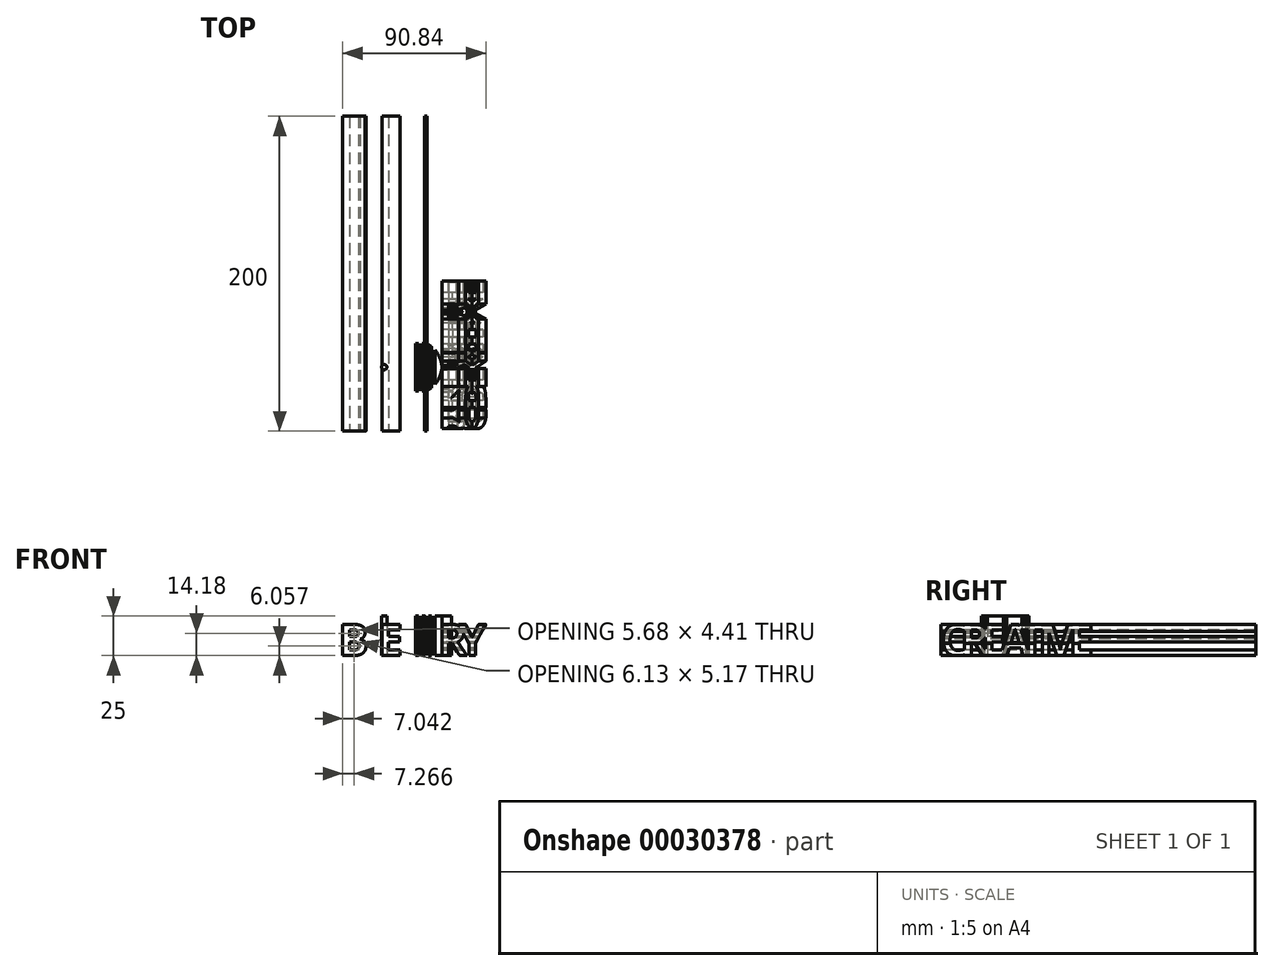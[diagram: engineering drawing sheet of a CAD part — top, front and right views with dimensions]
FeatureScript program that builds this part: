
annotation { "Feature Type Name" : "Feature", "Feature Type Description" : "" }
export const myFeature = defineFeature(function(context is Context, id is Id, definition is map)
    precondition{}
    {
        {
            var Q0;
            Q0=qCreatedBy(makeId("Front.planeOp"),FACE);
            var sketch = newSketch(context, id + "F0", { "sketchPlane" : qUnion([Q0])});
            skText(sketch, "E0", { "text": "B", "fontName": "OpenSans-Bold.ttf"});
            skText(sketch, "E1", { "text": "E", "fontName": "OpenSans-Bold.ttf"});
            skText(sketch, "E2", { "text": "E", "fontName": "OpenSans-Bold.ttf"});
            skText(sketch, "E3", { "text": "V", "fontName": "OpenSans-Bold.ttf"});
            skText(sketch, "E4", { "text": "E", "fontName": "OpenSans-Bold.ttf"});
            skText(sketch, "E5", { "text": "R", "fontName": "OpenSans-Bold.ttf"});
            skText(sketch, "E6", { "text": "Y", "fontName": "OpenSans-Bold.ttf"});
            const initialGuessF0  = {"E0": [0, 0, 1, 0, 0.02], "E1": [0.014, 0, 1, 0, 0.02], "E2": [0.025, 0, 1, 0, 0.02], "E3": [0.038, 0, 1, 0, 0.02], "E4": [0.052, 0, 1, 0, 0.02], "E5": [0.063, 0, 1, 0, 0.02], "E6": [0.076, 0, 1, 0, 0.02]};
            skSetInitialGuess(sketch, initialGuessF0);
            skSolve(sketch);
        }
        {
            var Q0;
            Q0=makeQuery(id+"F0.imprint","IMPRINT",FACE,{"disambiguationData":[TD([[makeQuery(id+"F0.imprint","IMPRINT",EDGE,{"derivedFrom":sQuery(id+"F0.wireOp",EDGE,"E0.sketch_text.stroke-0")}),-1.0]])]});
            var Q1;
            {var subQ7=sQuery(id+"F0.wireOp",EDGE,"E1.sketch_text.stroke-0");Q1=makeQuery(id+"F0.imprint","IMPRINT",FACE,{"disambiguationData":[TD([[makeQuery(id+"F0.imprint","IMPRINT",EDGE,{"derivedFrom":subQ7}),-1.0]])]});}
            var Q2;
            {var subQ1=sQuery(id+"F0.wireOp",EDGE,"E0.sketch_text.stroke-7");var subQ3=sQuery(id+"F0.wireOp",EDGE,"E0.sketch_text.stroke-8");var subQ5=makeQuery(id+"F0.imprint","INTERSECT",VERTEX,{"derivedFrom":[subQ1,subQ3]});Q2=makeQuery(id+"F0.imprint","IMPRINT",FACE,{"disambiguationData":[TD([[makeQuery(id+"F0.imprint","IMPRINT",EDGE,{"disambiguationData":[TD([[subQ5,1.0]])],"derivedFrom":subQ1}),-1.0]])]});}
            var Q3;
            {var subQ1=sQuery(id+"F0.wireOp",EDGE,"E0.sketch_text.stroke-3");var subQ3=sQuery(id+"F0.wireOp",EDGE,"E0.sketch_text.stroke-2");var subQ5=makeQuery(id+"F0.imprint","INTERSECT",VERTEX,{"derivedFrom":[subQ3,subQ1]});Q3=makeQuery(id+"F0.imprint","IMPRINT",FACE,{"disambiguationData":[TD([[makeQuery(id+"F0.imprint","IMPRINT",EDGE,{"disambiguationData":[TD([[subQ5,1.0]])],"derivedFrom":subQ3}),-1.0]])]});}
            var Q4;
            {var subQ7=sQuery(id+"F0.wireOp",EDGE,"E1.sketch_text.stroke-3");Q4=makeQuery(id+"F0.imprint","IMPRINT",FACE,{"disambiguationData":[TD([[makeQuery(id+"F0.imprint","IMPRINT",EDGE,{"derivedFrom":subQ7}),1.0]])]});}
            var Q5;
            {var subQ1=sQuery(id+"F0.wireOp",EDGE,"E1.sketch_text.stroke-3");Q5=makeQuery(id+"F0.imprint","IMPRINT",FACE,{"disambiguationData":[TD([[makeQuery(id+"F0.imprint","IMPRINT",EDGE,{"derivedFrom":subQ1}),-1.0]])]});}
            var Q6;
            {var subQ5=sQuery(id+"F0.wireOp",EDGE,"E1.sketch_text.stroke-11");Q6=makeQuery(id+"F0.imprint","IMPRINT",FACE,{"disambiguationData":[TD([[makeQuery(id+"F0.imprint","IMPRINT",EDGE,{"derivedFrom":subQ5}),-1.0]])]});}
            var Q7;
            {var subQ3=sQuery(id+"F0.wireOp",EDGE,"E3.sketch_text.stroke-0");Q7=makeQuery(id+"F0.imprint","IMPRINT",FACE,{"disambiguationData":[TD([[makeQuery(id+"F0.imprint","IMPRINT",EDGE,{"derivedFrom":subQ3}),-1.0]])]});}
            var Q8;
            {var subQ0=sQuery(id+"F0.wireOp",EDGE,"E3.sketch_text.stroke-4");var subQ1=sQuery(id+"F0.wireOp",EDGE,"E2.sketch_text.stroke-3");var subQ2=makeQuery(id+"F0.imprint","INTERSECT",VERTEX,{"derivedFrom":[subQ1,subQ0]});Q8=makeQuery(id+"F0.imprint","IMPRINT",FACE,{"disambiguationData":[TD([[makeQuery(id+"F0.imprint","IMPRINT",EDGE,{"disambiguationData":[TD([[subQ2,-1.0]])],"derivedFrom":subQ1}),-1.0]])]});}
            var Q9;
            {var subQ0=sQuery(id+"F0.wireOp",EDGE,"E4.sketch_text.stroke-2");var subQ1=sQuery(id+"F0.wireOp",EDGE,"E3.sketch_text.stroke-1");var subQ2=makeQuery(id+"F0.imprint","INTERSECT",VERTEX,{"derivedFrom":[subQ1,subQ0]});Q9=makeQuery(id+"F0.imprint","IMPRINT",FACE,{"disambiguationData":[TD([[makeQuery(id+"F0.imprint","IMPRINT",EDGE,{"disambiguationData":[TD([[subQ2,-1.0]])],"derivedFrom":subQ1}),-1.0]])]});}
            var Q10;
            {var subQ7=sQuery(id+"F0.wireOp",EDGE,"E4.sketch_text.stroke-0");Q10=makeQuery(id+"F0.imprint","IMPRINT",FACE,{"disambiguationData":[TD([[makeQuery(id+"F0.imprint","IMPRINT",EDGE,{"derivedFrom":subQ7}),-1.0]])]});}
            var Q11;
            {var subQ1=sQuery(id+"F0.wireOp",EDGE,"E4.sketch_text.stroke-3");Q11=makeQuery(id+"F0.imprint","IMPRINT",FACE,{"disambiguationData":[TD([[makeQuery(id+"F0.imprint","IMPRINT",EDGE,{"derivedFrom":subQ1}),-1.0]])]});}
            var Q12;
            {var subQ0=sQuery(id+"F0.wireOp",EDGE,"E4.sketch_text.stroke-3");Q12=makeQuery(id+"F0.imprint","IMPRINT",FACE,{"disambiguationData":[TD([[makeQuery(id+"F0.imprint","IMPRINT",EDGE,{"derivedFrom":subQ0}),1.0]])]});}
            var Q13;
            {var subQ5=sQuery(id+"F0.wireOp",EDGE,"E4.sketch_text.stroke-11");Q13=makeQuery(id+"F0.imprint","IMPRINT",FACE,{"disambiguationData":[TD([[makeQuery(id+"F0.imprint","IMPRINT",EDGE,{"derivedFrom":subQ5}),-1.0]])]});}
            var Q14;
            {var subQ3=sQuery(id+"F0.wireOp",EDGE,"E5.sketch_text.stroke-12");Q14=makeQuery(id+"F0.imprint","IMPRINT",FACE,{"disambiguationData":[TD([[makeQuery(id+"F0.imprint","IMPRINT",EDGE,{"derivedFrom":subQ3}),-1.0]])]});}
            var Q15;
            {var subQ7=sQuery(id+"F0.wireOp",EDGE,"E5.sketch_text.stroke-12");Q15=makeQuery(id+"F0.imprint","IMPRINT",FACE,{"disambiguationData":[TD([[makeQuery(id+"F0.imprint","IMPRINT",EDGE,{"derivedFrom":subQ7}),1.0]])]});}
            extrude(context, id + "F1", {"entities" : qUnion([Q0, Q1, Q2, Q3, Q4, Q5, Q6, Q7, Q8, Q9, Q10, Q11, Q12, Q13, Q14, Q15]), "oppositeDirection" : true, "depth" : 200 * mm});
        }
        {
            var Q0;
            Q0=qCreatedBy(makeId("Right.planeOp"),FACE);
            var sketch = newSketch(context, id + "F2", { "sketchPlane" : qUnion([Q0])});
            skText(sketch, "E7", { "text": "C", "fontName": "OpenSans-Bold.ttf"});
            skText(sketch, "E8", { "text": "R", "fontName": "OpenSans-Bold.ttf"});
            skText(sketch, "E9", { "text": "E", "fontName": "OpenSans-Bold.ttf"});
            skText(sketch, "E10", { "text": "A", "fontName": "OpenSans-Bold.ttf"});
            skText(sketch, "E11", { "text": "T", "fontName": "OpenSans-Bold.ttf"});
            skText(sketch, "E12", { "text": "I", "fontName": "OpenSans-Bold.ttf"});
            skText(sketch, "E13", { "text": "V", "fontName": "OpenSans-Bold.ttf"});
            skText(sketch, "E14", { "text": "E", "fontName": "OpenSans-Bold.ttf"});
            const initialGuessF2  = {"E7": [0, 0, 1, 0, 0.02], "E8": [0.01265, 0, 1, 0, 0.02], "E9": [0.02573, 0, 1, 0, 0.02], "E10": [0.03756, 0, 1, 0, 0.02], "E11": [0.04955, 0, 1, 0, 0.02], "E12": [0.062, 0, 1, 0, 0.02], "E13": [0.06685, 0, 1, 0, 0.02], "E14": [0.0813, 0, 1, 0, 0.02]};
            skSetInitialGuess(sketch, initialGuessF2);
            skSolve(sketch);
        }
        {
            var Q0;
            Q0 = qSketchRegion(id + "F2", true);
            var Q1;
            {var subQ5=sQuery(id+"F2.wireOp",EDGE,"E7.sketch_text.stroke-12");Q1=makeQuery(id+"F2.imprint","IMPRINT",FACE,{"disambiguationData":[TD([[makeQuery(id+"F2.imprint","IMPRINT",EDGE,{"derivedFrom":subQ5}),-1.0]])]});}
            var Q2;
            {var subQ1=sQuery(id+"F2.wireOp",EDGE,"E8.sketch_text.stroke-13");var subQ3=sQuery(id+"F2.wireOp",EDGE,"E8.sketch_text.stroke-12");var subQ5=makeQuery(id+"F2.imprint","INTERSECT",VERTEX,{"derivedFrom":[subQ3,subQ1]});Q2=makeQuery(id+"F2.imprint","IMPRINT",FACE,{"disambiguationData":[TD([[makeQuery(id+"F2.imprint","IMPRINT",EDGE,{"disambiguationData":[TD([[subQ5,1.0]])],"derivedFrom":subQ3}),-1.0]])]});}
            extrude(context, id + "F3", {"entities" : qUnion([Q0, Q1, Q2]), "depth" : 200 * mm});
        }
        {
            var Q0;
            Q0=makeQuery(id+"F1.opExtrude","SWEPT_BODY",BODY,{"disambiguationData":[OSD([sQuery(id+"F0.wireOp",EDGE,"E0.sketch_text.stroke-0"),sQuery(id+"F0.wireOp",EDGE,"E0.sketch_text.stroke-1"),sQuery(id+"F0.wireOp",EDGE,"E0.sketch_text.stroke-2"),sQuery(id+"F0.wireOp",EDGE,"E0.sketch_text.stroke-3"),sQuery(id+"F0.wireOp",EDGE,"E0.sketch_text.stroke-4"),sQuery(id+"F0.wireOp",EDGE,"E0.sketch_text.stroke-5"),sQuery(id+"F0.wireOp",EDGE,"E0.sketch_text.stroke-6"),sQuery(id+"F0.wireOp",EDGE,"E0.sketch_text.stroke-7"),sQuery(id+"F0.wireOp",EDGE,"E0.sketch_text.stroke-8"),sQuery(id+"F0.wireOp",EDGE,"E0.sketch_text.stroke-9"),sQuery(id+"F0.wireOp",EDGE,"E0.sketch_text.stroke-10"),sQuery(id+"F0.wireOp",EDGE,"E0.sketch_text.stroke-11"),sQuery(id+"F0.wireOp",EDGE,"E0.sketch_text.stroke-12"),sQuery(id+"F0.wireOp",EDGE,"E0.sketch_text.stroke-13"),sQuery(id+"F0.wireOp",EDGE,"E0.sketch_text.stroke-14"),sQuery(id+"F0.wireOp",EDGE,"E0.sketch_text.stroke-15"),sQuery(id+"F0.wireOp",EDGE,"E0.sketch_text.stroke-16"),sQuery(id+"F0.wireOp",EDGE,"E0.sketch_text.stroke-17"),sQuery(id+"F0.wireOp",EDGE,"E0.sketch_text.stroke-18"),sQuery(id+"F0.wireOp",EDGE,"E0.sketch_text.stroke-19"),sQuery(id+"F0.wireOp",EDGE,"E0.sketch_text.stroke-20"),sQuery(id+"F0.wireOp",EDGE,"E0.sketch_text.stroke-21"),sQuery(id+"F0.wireOp",EDGE,"E0.sketch_text.stroke-22"),sQuery(id+"F0.wireOp",EDGE,"E0.sketch_text.stroke-23"),sQuery(id+"F0.wireOp",EDGE,"E0.sketch_text.stroke-24"),sQuery(id+"F0.wireOp",EDGE,"E1.sketch_text.stroke-0"),sQuery(id+"F0.wireOp",EDGE,"E1.sketch_text.stroke-1"),sQuery(id+"F0.wireOp",EDGE,"E1.sketch_text.stroke-2"),sQuery(id+"F0.wireOp",EDGE,"E1.sketch_text.stroke-4"),sQuery(id+"F0.wireOp",EDGE,"E1.sketch_text.stroke-5"),sQuery(id+"F0.wireOp",EDGE,"E1.sketch_text.stroke-6"),sQuery(id+"F0.wireOp",EDGE,"E1.sketch_text.stroke-7"),sQuery(id+"F0.wireOp",EDGE,"E1.sketch_text.stroke-8"),sQuery(id+"F0.wireOp",EDGE,"E1.sketch_text.stroke-9"),sQuery(id+"F0.wireOp",EDGE,"E1.sketch_text.stroke-10"),sQuery(id+"F0.wireOp",EDGE,"E2.sketch_text.stroke-0"),sQuery(id+"F0.wireOp",EDGE,"E2.sketch_text.stroke-1"),sQuery(id+"F0.wireOp",EDGE,"E2.sketch_text.stroke-2"),sQuery(id+"F0.wireOp",EDGE,"E2.sketch_text.stroke-3"),sQuery(id+"F0.wireOp",EDGE,"E2.sketch_text.stroke-4"),sQuery(id+"F0.wireOp",EDGE,"E2.sketch_text.stroke-5"),sQuery(id+"F0.wireOp",EDGE,"E2.sketch_text.stroke-6"),sQuery(id+"F0.wireOp",EDGE,"E2.sketch_text.stroke-7"),sQuery(id+"F0.wireOp",EDGE,"E2.sketch_text.stroke-8"),sQuery(id+"F0.wireOp",EDGE,"E2.sketch_text.stroke-9"),sQuery(id+"F0.wireOp",EDGE,"E2.sketch_text.stroke-10"),sQuery(id+"F0.wireOp",EDGE,"E2.sketch_text.stroke-11"),sQuery(id+"F0.wireOp",EDGE,"E3.sketch_text.stroke-0"),sQuery(id+"F0.wireOp",EDGE,"E3.sketch_text.stroke-1"),sQuery(id+"F0.wireOp",EDGE,"E3.sketch_text.stroke-2"),sQuery(id+"F0.wireOp",EDGE,"E3.sketch_text.stroke-3"),sQuery(id+"F0.wireOp",EDGE,"E3.sketch_text.stroke-4"),sQuery(id+"F0.wireOp",EDGE,"E3.sketch_text.stroke-5"),sQuery(id+"F0.wireOp",EDGE,"E3.sketch_text.stroke-6"),sQuery(id+"F0.wireOp",EDGE,"E3.sketch_text.stroke-7"),sQuery(id+"F0.wireOp",EDGE,"E3.sketch_text.stroke-8"),sQuery(id+"F0.wireOp",EDGE,"E3.sketch_text.stroke-9"),sQuery(id+"F0.wireOp",EDGE,"E4.sketch_text.stroke-0"),sQuery(id+"F0.wireOp",EDGE,"E4.sketch_text.stroke-1"),sQuery(id+"F0.wireOp",EDGE,"E4.sketch_text.stroke-2"),sQuery(id+"F0.wireOp",EDGE,"E4.sketch_text.stroke-4"),sQuery(id+"F0.wireOp",EDGE,"E4.sketch_text.stroke-5"),sQuery(id+"F0.wireOp",EDGE,"E4.sketch_text.stroke-6"),sQuery(id+"F0.wireOp",EDGE,"E4.sketch_text.stroke-7"),sQuery(id+"F0.wireOp",EDGE,"E4.sketch_text.stroke-8"),sQuery(id+"F0.wireOp",EDGE,"E4.sketch_text.stroke-9"),sQuery(id+"F0.wireOp",EDGE,"E4.sketch_text.stroke-10"),sQuery(id+"F0.wireOp",EDGE,"E5.sketch_text.stroke-0"),sQuery(id+"F0.wireOp",EDGE,"E5.sketch_text.stroke-1"),sQuery(id+"F0.wireOp",EDGE,"E5.sketch_text.stroke-2"),sQuery(id+"F0.wireOp",EDGE,"E5.sketch_text.stroke-3"),sQuery(id+"F0.wireOp",EDGE,"E5.sketch_text.stroke-4"),sQuery(id+"F0.wireOp",EDGE,"E5.sketch_text.stroke-5"),sQuery(id+"F0.wireOp",EDGE,"E5.sketch_text.stroke-6"),sQuery(id+"F0.wireOp",EDGE,"E5.sketch_text.stroke-7"),sQuery(id+"F0.wireOp",EDGE,"E5.sketch_text.stroke-8"),sQuery(id+"F0.wireOp",EDGE,"E5.sketch_text.stroke-9"),sQuery(id+"F0.wireOp",EDGE,"E5.sketch_text.stroke-10"),sQuery(id+"F0.wireOp",EDGE,"E5.sketch_text.stroke-11"),sQuery(id+"F0.wireOp",EDGE,"E5.sketch_text.stroke-13"),sQuery(id+"F0.wireOp",EDGE,"E5.sketch_text.stroke-14"),sQuery(id+"F0.wireOp",EDGE,"E5.sketch_text.stroke-15"),sQuery(id+"F0.wireOp",EDGE,"E5.sketch_text.stroke-16"),sQuery(id+"F0.wireOp",EDGE,"E5.sketch_text.stroke-17"),sQuery(id+"F0.wireOp",EDGE,"E5.sketch_text.stroke-18"),sQuery(id+"F0.wireOp",EDGE,"E6.sketch_text.stroke-0"),sQuery(id+"F0.wireOp",EDGE,"E6.sketch_text.stroke-1"),sQuery(id+"F0.wireOp",EDGE,"E6.sketch_text.stroke-2"),sQuery(id+"F0.wireOp",EDGE,"E6.sketch_text.stroke-3"),sQuery(id+"F0.wireOp",EDGE,"E6.sketch_text.stroke-4"),sQuery(id+"F0.wireOp",EDGE,"E6.sketch_text.stroke-5"),sQuery(id+"F0.wireOp",EDGE,"E6.sketch_text.stroke-6"),sQuery(id+"F0.wireOp",EDGE,"E6.sketch_text.stroke-7"),sQuery(id+"F0.wireOp",EDGE,"E6.sketch_text.stroke-8")])]});
            var Q1;
            Q1=makeQuery(id+"F3.opExtrude","SWEPT_BODY",BODY,{"disambiguationData":[OSD([sQuery(id+"F2.wireOp",EDGE,"E7.sketch_text.stroke-0"),sQuery(id+"F2.wireOp",EDGE,"E7.sketch_text.stroke-1"),sQuery(id+"F2.wireOp",EDGE,"E7.sketch_text.stroke-2"),sQuery(id+"F2.wireOp",EDGE,"E7.sketch_text.stroke-3"),sQuery(id+"F2.wireOp",EDGE,"E7.sketch_text.stroke-5"),sQuery(id+"F2.wireOp",EDGE,"E7.sketch_text.stroke-6"),sQuery(id+"F2.wireOp",EDGE,"E7.sketch_text.stroke-7"),sQuery(id+"F2.wireOp",EDGE,"E7.sketch_text.stroke-8"),sQuery(id+"F2.wireOp",EDGE,"E7.sketch_text.stroke-9"),sQuery(id+"F2.wireOp",EDGE,"E7.sketch_text.stroke-10"),sQuery(id+"F2.wireOp",EDGE,"E7.sketch_text.stroke-11"),sQuery(id+"F2.wireOp",EDGE,"E7.sketch_text.stroke-13"),sQuery(id+"F2.wireOp",EDGE,"E7.sketch_text.stroke-14"),sQuery(id+"F2.wireOp",EDGE,"E8.sketch_text.stroke-0"),sQuery(id+"F2.wireOp",EDGE,"E8.sketch_text.stroke-1"),sQuery(id+"F2.wireOp",EDGE,"E8.sketch_text.stroke-2"),sQuery(id+"F2.wireOp",EDGE,"E8.sketch_text.stroke-3"),sQuery(id+"F2.wireOp",EDGE,"E8.sketch_text.stroke-4"),sQuery(id+"F2.wireOp",EDGE,"E8.sketch_text.stroke-5"),sQuery(id+"F2.wireOp",EDGE,"E8.sketch_text.stroke-6"),sQuery(id+"F2.wireOp",EDGE,"E8.sketch_text.stroke-7"),sQuery(id+"F2.wireOp",EDGE,"E8.sketch_text.stroke-8"),sQuery(id+"F2.wireOp",EDGE,"E8.sketch_text.stroke-9"),sQuery(id+"F2.wireOp",EDGE,"E8.sketch_text.stroke-10"),sQuery(id+"F2.wireOp",EDGE,"E8.sketch_text.stroke-11"),sQuery(id+"F2.wireOp",EDGE,"E8.sketch_text.stroke-12"),sQuery(id+"F2.wireOp",EDGE,"E8.sketch_text.stroke-13"),sQuery(id+"F2.wireOp",EDGE,"E8.sketch_text.stroke-14"),sQuery(id+"F2.wireOp",EDGE,"E8.sketch_text.stroke-15"),sQuery(id+"F2.wireOp",EDGE,"E8.sketch_text.stroke-16"),sQuery(id+"F2.wireOp",EDGE,"E8.sketch_text.stroke-17"),sQuery(id+"F2.wireOp",EDGE,"E8.sketch_text.stroke-18"),sQuery(id+"F2.wireOp",EDGE,"E9.sketch_text.stroke-0"),sQuery(id+"F2.wireOp",EDGE,"E9.sketch_text.stroke-1"),sQuery(id+"F2.wireOp",EDGE,"E9.sketch_text.stroke-2"),sQuery(id+"F2.wireOp",EDGE,"E9.sketch_text.stroke-3"),sQuery(id+"F2.wireOp",EDGE,"E9.sketch_text.stroke-4"),sQuery(id+"F2.wireOp",EDGE,"E9.sketch_text.stroke-5"),sQuery(id+"F2.wireOp",EDGE,"E9.sketch_text.stroke-6"),sQuery(id+"F2.wireOp",EDGE,"E9.sketch_text.stroke-7"),sQuery(id+"F2.wireOp",EDGE,"E9.sketch_text.stroke-8"),sQuery(id+"F2.wireOp",EDGE,"E9.sketch_text.stroke-9"),sQuery(id+"F2.wireOp",EDGE,"E9.sketch_text.stroke-10"),sQuery(id+"F2.wireOp",EDGE,"E10.sketch_text.stroke-0"),sQuery(id+"F2.wireOp",EDGE,"E10.sketch_text.stroke-1"),sQuery(id+"F2.wireOp",EDGE,"E10.sketch_text.stroke-2"),sQuery(id+"F2.wireOp",EDGE,"E10.sketch_text.stroke-3"),sQuery(id+"F2.wireOp",EDGE,"E10.sketch_text.stroke-4"),sQuery(id+"F2.wireOp",EDGE,"E10.sketch_text.stroke-5"),sQuery(id+"F2.wireOp",EDGE,"E10.sketch_text.stroke-6"),sQuery(id+"F2.wireOp",EDGE,"E10.sketch_text.stroke-7"),sQuery(id+"F2.wireOp",EDGE,"E10.sketch_text.stroke-8"),sQuery(id+"F2.wireOp",EDGE,"E10.sketch_text.stroke-9"),sQuery(id+"F2.wireOp",EDGE,"E10.sketch_text.stroke-10"),sQuery(id+"F2.wireOp",EDGE,"E10.sketch_text.stroke-11"),sQuery(id+"F2.wireOp",EDGE,"E11.sketch_text.stroke-0"),sQuery(id+"F2.wireOp",EDGE,"E11.sketch_text.stroke-1"),sQuery(id+"F2.wireOp",EDGE,"E11.sketch_text.stroke-2"),sQuery(id+"F2.wireOp",EDGE,"E11.sketch_text.stroke-3"),sQuery(id+"F2.wireOp",EDGE,"E11.sketch_text.stroke-4"),sQuery(id+"F2.wireOp",EDGE,"E11.sketch_text.stroke-6"),sQuery(id+"F2.wireOp",EDGE,"E11.sketch_text.stroke-7"),sQuery(id+"F2.wireOp",EDGE,"E12.sketch_text.stroke-0"),sQuery(id+"F2.wireOp",EDGE,"E12.sketch_text.stroke-1"),sQuery(id+"F2.wireOp",EDGE,"E12.sketch_text.stroke-2"),sQuery(id+"F2.wireOp",EDGE,"E12.sketch_text.stroke-3"),sQuery(id+"F2.wireOp",EDGE,"E13.sketch_text.stroke-0"),sQuery(id+"F2.wireOp",EDGE,"E13.sketch_text.stroke-1"),sQuery(id+"F2.wireOp",EDGE,"E13.sketch_text.stroke-2"),sQuery(id+"F2.wireOp",EDGE,"E13.sketch_text.stroke-3"),sQuery(id+"F2.wireOp",EDGE,"E13.sketch_text.stroke-4"),sQuery(id+"F2.wireOp",EDGE,"E13.sketch_text.stroke-5"),sQuery(id+"F2.wireOp",EDGE,"E13.sketch_text.stroke-6"),sQuery(id+"F2.wireOp",EDGE,"E13.sketch_text.stroke-7"),sQuery(id+"F2.wireOp",EDGE,"E13.sketch_text.stroke-8"),sQuery(id+"F2.wireOp",EDGE,"E13.sketch_text.stroke-9"),sQuery(id+"F2.wireOp",EDGE,"E14.sketch_text.stroke-0"),sQuery(id+"F2.wireOp",EDGE,"E14.sketch_text.stroke-1"),sQuery(id+"F2.wireOp",EDGE,"E14.sketch_text.stroke-2"),sQuery(id+"F2.wireOp",EDGE,"E14.sketch_text.stroke-3"),sQuery(id+"F2.wireOp",EDGE,"E14.sketch_text.stroke-4"),sQuery(id+"F2.wireOp",EDGE,"E14.sketch_text.stroke-5"),sQuery(id+"F2.wireOp",EDGE,"E14.sketch_text.stroke-6"),sQuery(id+"F2.wireOp",EDGE,"E14.sketch_text.stroke-7"),sQuery(id+"F2.wireOp",EDGE,"E14.sketch_text.stroke-8"),sQuery(id+"F2.wireOp",EDGE,"E14.sketch_text.stroke-9"),sQuery(id+"F2.wireOp",EDGE,"E14.sketch_text.stroke-10"),sQuery(id+"F2.wireOp",EDGE,"E14.sketch_text.stroke-11")])]});
            booleanBodies(context, id + "F4", {"operationType" : BooleanOperationType.INTERSECTION, "tools" : qUnion([Q0, Q1])});
        }
        {
            var Q0;
            Q0=qCreatedBy(makeId("Top.planeOp"),FACE);
            var sketch = newSketch(context, id + "F5", { "sketchPlane" : qUnion([Q0])});
            skArc(sketch, "E15", {"start": v(46.65, 55.83) * mm, "mid": v(56.09, 65.27) * mm, "end": v(46.65, 74.72) * mm});
            skArc(sketch, "E16", {"start": v(51.42, 55.83) * mm, "mid": v(60.87, 65.27) * mm, "end": v(51.42, 74.72) * mm});
            skLineSegment(sketch, "E17", {"start": v(46.65, 74.72) * mm, "end": v(46.65, 55.83) * mm});
            skLineSegment(sketch, "E18", {"start": v(51.42, 74.72) * mm, "end": v(51.42, 55.83) * mm});
            skPoint(sketch, "E19", {"position": v(23.92, 40.63) * mm});
            skCircle(sketch, "E20", {"center": v(35, 40.6) * mm, "radius": 8.73 * mm});
            skPoint(sketch, "E20.first.point", {"position": v(29.73, 47.56) * mm});
            skPoint(sketch, "E20.second.point", {"position": v(42.47, 45.11) * mm});
            skPoint(sketch, "E20.third.point", {"position": v(34.93, 31.86) * mm});
            skCircle(sketch, "E21", {"center": v(28.83, 40.66) * mm, "radius": 1.68 * mm});
            skPoint(sketch, "E21.first.point", {"position": v(28.33, 42.26) * mm});
            skPoint(sketch, "E21.second.point", {"position": v(29.05, 39) * mm});
            skPoint(sketch, "E21.third.point", {"position": v(30.48, 40.32) * mm});
            skLineSegment(sketch, "E22.bottom", {"start": v(46.65, 25.63) * mm, "end": v(48.85, 25.63) * mm});
            skLineSegment(sketch, "E22.top", {"start": v(46.65, 55.83) * mm, "end": v(48.85, 55.83) * mm});
            skLineSegment(sketch, "E22.left", {"start": v(46.65, 25.63) * mm, "end": v(46.65, 55.83) * mm});
            skLineSegment(sketch, "E22.right", {"start": v(48.85, 25.63) * mm, "end": v(48.85, 55.83) * mm});
            skPoint(sketch, "E23.firstSnap0", {"position": v(47.75, 25.63) * mm});
            skLineSegment(sketch, "E23.bottom", {"start": v(50.79, 25.63) * mm, "end": v(53, 25.63) * mm});
            skLineSegment(sketch, "E23.top", {"start": v(50.79, 55.83) * mm, "end": v(53, 55.83) * mm});
            skLineSegment(sketch, "E23.left", {"start": v(50.79, 25.63) * mm, "end": v(50.79, 55.83) * mm});
            skLineSegment(sketch, "E23.right", {"start": v(53, 25.63) * mm, "end": v(53, 55.83) * mm});
            skLineSegment(sketch, "E24.bottom", {"start": v(54.8, 55.83) * mm, "end": v(57, 55.83) * mm});
            skLineSegment(sketch, "E24.top", {"start": v(54.8, 25.63) * mm, "end": v(57, 25.63) * mm});
            skLineSegment(sketch, "E24.left", {"start": v(54.8, 55.83) * mm, "end": v(54.8, 25.63) * mm});
            skLineSegment(sketch, "E24.right", {"start": v(57, 55.83) * mm, "end": v(57, 25.63) * mm});
            skLineSegment(sketch, "E25.bottom", {"start": v(58.95, 55.83) * mm, "end": v(61.15, 55.83) * mm});
            skLineSegment(sketch, "E25.top", {"start": v(58.95, 25.63) * mm, "end": v(61.15, 25.63) * mm});
            skLineSegment(sketch, "E25.left", {"start": v(58.95, 55.83) * mm, "end": v(58.95, 25.63) * mm});
            skLineSegment(sketch, "E25.right", {"start": v(61.15, 55.83) * mm, "end": v(61.15, 25.63) * mm});
            skLineSegment(sketch, "E26.bottom", {"start": v(23.92, 55.83) * mm, "end": v(65.46, 55.83) * mm});
            skLineSegment(sketch, "E26.top", {"start": v(23.92, 25.65) * mm, "end": v(65.46, 25.65) * mm});
            skLineSegment(sketch, "E26.left", {"start": v(23.92, 55.83) * mm, "end": v(23.92, 25.65) * mm});
            skLineSegment(sketch, "E26.right", {"start": v(65.46, 55.83) * mm, "end": v(65.46, 25.65) * mm});
            skLineSegment(sketch, "E27.left", {"start": v(64.62, 41.68) * mm, "end": v(64.62, 39.63) * mm});
            skFitSpline(sketch, "E28", {"points": [v(23.92, 40.63) * mm, v(36.7, 55.83) * mm], "startDerivative": vector(0, 13.57) * mm, "endDerivative": vector(26.12, 0) * mm});
            skLineSegment(sketch, "E29", {"start": v(23.92, 40.63) * mm, "end": v(64.62, 40.66) * mm, "construction": true});
            skLineSegment(sketch, "E30", {"start": v(44.69, 25.65) * mm, "end": v(44.69, 55.83) * mm, "construction": true});
            skFitSpline(sketch, "E31.MirrorCS", {"points": [v(65.46, 40.63) * mm, v(52.67, 55.83) * mm], "startDerivative": vector(0, 13.57) * mm, "endDerivative": vector(-26.12, 0) * mm});
            skFitSpline(sketch, "E32.MirrorCS", {"points": [v(23.92, 40.63) * mm, v(36.73, 25.44) * mm], "startDerivative": vector(0.02, -13.57) * mm, "endDerivative": vector(26.12, 0.04) * mm});
            skFitSpline(sketch, "E33.MirrorCS", {"points": [v(65.46, 40.69) * mm, v(52.7, 25.47) * mm], "startDerivative": vector(0.02, -13.57) * mm, "endDerivative": vector(-26.12, -0.04) * mm});
            skFitSpline(sketch, "E34", {"points": [v(64.62, 41.68) * mm, v(71.73, 40.62) * mm], "startDerivative": vector(9.44, 0) * mm, "endDerivative": vector(2.06, -4.11) * mm});
            skFitSpline(sketch, "E35.MirrorCS", {"points": [v(64.62, 39.63) * mm, v(71.73, 40.7) * mm], "startDerivative": vector(9.44, 0.01) * mm, "endDerivative": vector(2.05, 4.11) * mm});
            skSolve(sketch);
        }
        {
            var Q0;
            {var subQ4=sQuery(id+"F5.wireOp",EDGE,"E17");Q0=makeQuery(id+"F5.imprint","IMPRINT",FACE,{"disambiguationData":[TD([[makeQuery(id+"F5.imprint","IMPRINT",EDGE,{"derivedFrom":subQ4}),1.0]])]});}
            var Q1;
            {var subQ3=sQuery(id+"F5.wireOp",EDGE,"E16");Q1=makeQuery(id+"F5.imprint","IMPRINT",FACE,{"disambiguationData":[TD([[makeQuery(id+"F5.imprint","IMPRINT",EDGE,{"derivedFrom":subQ3}),1.0]])]});}
            var Q2;
            {var subQ4=sQuery(id+"F5.wireOp",EDGE,"E27.bottom");Q2=makeQuery(id+"F5.imprint","IMPRINT",FACE,{"disambiguationData":[TD([[makeQuery(id+"F5.imprint","IMPRINT",EDGE,{"derivedFrom":subQ4}),-1.0]])]});}
            var Q3;
            {var subQ3=sQuery(id+"F5.wireOp",EDGE,"E24.right");var subQ5=sQuery(id+"F5.wireOp",EDGE,"E31.MirrorCS");var subQ7=makeQuery(id+"F5.imprint","INTERSECT",VERTEX,{"derivedFrom":[subQ3,subQ5]});Q3=makeQuery(id+"F5.imprint","IMPRINT",FACE,{"disambiguationData":[TD([[makeQuery(id+"F5.imprint","IMPRINT",EDGE,{"disambiguationData":[TD([[subQ7,-1.0]])],"derivedFrom":subQ3}),1.0]])]});}
            var Q4;
            {var subQ3=sQuery(id+"F5.wireOp",EDGE,"E26.top");var subQ7=sQuery(id+"F5.wireOp",EDGE,"E23.right");var subQ9=makeQuery(id+"F5.imprint","INTERSECT",VERTEX,{"derivedFrom":[subQ7,subQ3]});Q4=makeQuery(id+"F5.imprint","IMPRINT",FACE,{"disambiguationData":[TD([[makeQuery(id+"F5.imprint","IMPRINT",EDGE,{"disambiguationData":[TD([[subQ9,-1.0]])],"derivedFrom":subQ7}),-1.0]])]});}
            var Q5;
            {var subQ3=sQuery(id+"F5.wireOp",EDGE,"E22.right");var subQ5=sQuery(id+"F5.wireOp",EDGE,"E26.bottom");var subQ7=makeQuery(id+"F5.imprint","INTERSECT",VERTEX,{"derivedFrom":[subQ3,subQ5]});Q5=makeQuery(id+"F5.imprint","IMPRINT",FACE,{"disambiguationData":[TD([[makeQuery(id+"F5.imprint","IMPRINT",EDGE,{"disambiguationData":[TD([[subQ7,1.0]])],"derivedFrom":subQ3}),-1.0]])]});}
            var Q6;
            Q6=makeQuery(id+"F5.imprint","IMPRINT",FACE,{"disambiguationData":[TD([[makeQuery(id+"F5.imprint","IMPRINT",EDGE,{"derivedFrom":sQuery(id+"F5.wireOp",EDGE,"E20")}),-1.0]])]});
            var Q7;
            Q7=makeQuery(id+"F5.imprint","IMPRINT",FACE,{"disambiguationData":[TD([[makeQuery(id+"F5.imprint","IMPRINT",EDGE,{"derivedFrom":sQuery(id+"F5.wireOp",EDGE,"E21")}),1.0]])]});
            var Q8;
            {var subQ0=sQuery(id+"F5.wireOp",EDGE,"E18");var subQ1=sQuery(id+"F5.wireOp",EDGE,"E15");var subQ3=makeQuery(id+"F5.imprint","INTERSECT",VERTEX,{"disambiguationData":[OD(0.0)],"derivedFrom":[subQ1,subQ0]});Q8=makeQuery(id+"F5.imprint","IMPRINT",FACE,{"disambiguationData":[TD([[makeQuery(id+"F5.imprint","IMPRINT",EDGE,{"disambiguationData":[TD([[subQ3,1.0]])],"derivedFrom":subQ1}),1.0]])]});}
            var Q9;
            {var subQ1=sQuery(id+"F5.wireOp",EDGE,"E26.right");var subQ6=makeQuery(id+"F5.imprint","INTERSECT",VERTEX,{"derivedFrom":[subQ1,sQuery(id+"F5.wireOp",EDGE,"E31.MirrorCS")]});Q9=makeQuery(id+"F5.imprint","IMPRINT",FACE,{"disambiguationData":[TD([[makeQuery(id+"F5.imprint","IMPRINT",EDGE,{"disambiguationData":[TD([[subQ6,1.0]])],"derivedFrom":subQ1}),1.0]])]});}
            var Q10;
            {var subQ1=sQuery(id+"F5.wireOp",EDGE,"E25.right");var subQ4=sQuery(id+"F5.wireOp",EDGE,"E31.MirrorCS");var subQ6=makeQuery(id+"F5.imprint","INTERSECT",VERTEX,{"derivedFrom":[subQ1,subQ4]});Q10=makeQuery(id+"F5.imprint","IMPRINT",FACE,{"disambiguationData":[TD([[makeQuery(id+"F5.imprint","IMPRINT",EDGE,{"disambiguationData":[TD([[subQ6,-1.0]])],"derivedFrom":subQ1}),1.0]])]});}
            extrude(context, id + "F6", {"entities" : qUnion([Q0, Q1, Q2, Q3, Q4, Q5, Q6, Q7, Q8, Q9, Q10]), "depth" : 25 * mm});
        }
        {
            var Q0;
            Q0=makeQuery(id+"F6.opExtrude","SWEPT_BODY",BODY,{"disambiguationData":[OSD([sQuery(id+"F5.wireOp",EDGE,"E15"),sQuery(id+"F5.wireOp",EDGE,"E16"),sQuery(id+"F5.wireOp",EDGE,"E17"),sQuery(id+"F5.wireOp",EDGE,"E18")])]});
            var Q1;
            Q1=makeQuery(id+"F6.opExtrude","SWEPT_BODY",BODY,{"disambiguationData":[OSD([sQuery(id+"F5.wireOp",EDGE,"E20"),sQuery(id+"F5.wireOp",EDGE,"E22.left"),sQuery(id+"F5.wireOp",EDGE,"E26.bottom"),sQuery(id+"F5.wireOp",EDGE,"E26.top"),sQuery(id+"F5.wireOp",EDGE,"E28"),sQuery(id+"F5.wireOp",EDGE,"E32.MirrorCS")])]});
            var Q2;
            Q2=makeQuery(id+"F4.opBoolean","INTERSECT",BODY,{"derivedFrom":[makeQuery(id+"F1.opExtrude","SWEPT_BODY",BODY,{"disambiguationData":[OSD([sQuery(id+"F0.wireOp",EDGE,"E0.sketch_text.stroke-0"),sQuery(id+"F0.wireOp",EDGE,"E0.sketch_text.stroke-1"),sQuery(id+"F0.wireOp",EDGE,"E0.sketch_text.stroke-2"),sQuery(id+"F0.wireOp",EDGE,"E0.sketch_text.stroke-3"),sQuery(id+"F0.wireOp",EDGE,"E0.sketch_text.stroke-4"),sQuery(id+"F0.wireOp",EDGE,"E0.sketch_text.stroke-5"),sQuery(id+"F0.wireOp",EDGE,"E0.sketch_text.stroke-6"),sQuery(id+"F0.wireOp",EDGE,"E0.sketch_text.stroke-7"),sQuery(id+"F0.wireOp",EDGE,"E0.sketch_text.stroke-8"),sQuery(id+"F0.wireOp",EDGE,"E0.sketch_text.stroke-9"),sQuery(id+"F0.wireOp",EDGE,"E0.sketch_text.stroke-10"),sQuery(id+"F0.wireOp",EDGE,"E0.sketch_text.stroke-11"),sQuery(id+"F0.wireOp",EDGE,"E0.sketch_text.stroke-12"),sQuery(id+"F0.wireOp",EDGE,"E0.sketch_text.stroke-13"),sQuery(id+"F0.wireOp",EDGE,"E0.sketch_text.stroke-14"),sQuery(id+"F0.wireOp",EDGE,"E0.sketch_text.stroke-15"),sQuery(id+"F0.wireOp",EDGE,"E0.sketch_text.stroke-16"),sQuery(id+"F0.wireOp",EDGE,"E0.sketch_text.stroke-17"),sQuery(id+"F0.wireOp",EDGE,"E0.sketch_text.stroke-18"),sQuery(id+"F0.wireOp",EDGE,"E0.sketch_text.stroke-19"),sQuery(id+"F0.wireOp",EDGE,"E0.sketch_text.stroke-20"),sQuery(id+"F0.wireOp",EDGE,"E0.sketch_text.stroke-21"),sQuery(id+"F0.wireOp",EDGE,"E0.sketch_text.stroke-22"),sQuery(id+"F0.wireOp",EDGE,"E0.sketch_text.stroke-23"),sQuery(id+"F0.wireOp",EDGE,"E0.sketch_text.stroke-24"),sQuery(id+"F0.wireOp",EDGE,"E1.sketch_text.stroke-0"),sQuery(id+"F0.wireOp",EDGE,"E1.sketch_text.stroke-1"),sQuery(id+"F0.wireOp",EDGE,"E1.sketch_text.stroke-2"),sQuery(id+"F0.wireOp",EDGE,"E1.sketch_text.stroke-4"),sQuery(id+"F0.wireOp",EDGE,"E1.sketch_text.stroke-5"),sQuery(id+"F0.wireOp",EDGE,"E1.sketch_text.stroke-6"),sQuery(id+"F0.wireOp",EDGE,"E1.sketch_text.stroke-7"),sQuery(id+"F0.wireOp",EDGE,"E1.sketch_text.stroke-8"),sQuery(id+"F0.wireOp",EDGE,"E1.sketch_text.stroke-9"),sQuery(id+"F0.wireOp",EDGE,"E1.sketch_text.stroke-10"),sQuery(id+"F0.wireOp",EDGE,"E2.sketch_text.stroke-0"),sQuery(id+"F0.wireOp",EDGE,"E2.sketch_text.stroke-1"),sQuery(id+"F0.wireOp",EDGE,"E2.sketch_text.stroke-2"),sQuery(id+"F0.wireOp",EDGE,"E2.sketch_text.stroke-3"),sQuery(id+"F0.wireOp",EDGE,"E2.sketch_text.stroke-4"),sQuery(id+"F0.wireOp",EDGE,"E2.sketch_text.stroke-5"),sQuery(id+"F0.wireOp",EDGE,"E2.sketch_text.stroke-6"),sQuery(id+"F0.wireOp",EDGE,"E2.sketch_text.stroke-7"),sQuery(id+"F0.wireOp",EDGE,"E2.sketch_text.stroke-8"),sQuery(id+"F0.wireOp",EDGE,"E2.sketch_text.stroke-9"),sQuery(id+"F0.wireOp",EDGE,"E2.sketch_text.stroke-10"),sQuery(id+"F0.wireOp",EDGE,"E2.sketch_text.stroke-11"),sQuery(id+"F0.wireOp",EDGE,"E3.sketch_text.stroke-0"),sQuery(id+"F0.wireOp",EDGE,"E3.sketch_text.stroke-1"),sQuery(id+"F0.wireOp",EDGE,"E3.sketch_text.stroke-2"),sQuery(id+"F0.wireOp",EDGE,"E3.sketch_text.stroke-3"),sQuery(id+"F0.wireOp",EDGE,"E3.sketch_text.stroke-4"),sQuery(id+"F0.wireOp",EDGE,"E3.sketch_text.stroke-5"),sQuery(id+"F0.wireOp",EDGE,"E3.sketch_text.stroke-6"),sQuery(id+"F0.wireOp",EDGE,"E3.sketch_text.stroke-7"),sQuery(id+"F0.wireOp",EDGE,"E3.sketch_text.stroke-8"),sQuery(id+"F0.wireOp",EDGE,"E3.sketch_text.stroke-9"),sQuery(id+"F0.wireOp",EDGE,"E4.sketch_text.stroke-0"),sQuery(id+"F0.wireOp",EDGE,"E4.sketch_text.stroke-1"),sQuery(id+"F0.wireOp",EDGE,"E4.sketch_text.stroke-2"),sQuery(id+"F0.wireOp",EDGE,"E4.sketch_text.stroke-4"),sQuery(id+"F0.wireOp",EDGE,"E4.sketch_text.stroke-5"),sQuery(id+"F0.wireOp",EDGE,"E4.sketch_text.stroke-6"),sQuery(id+"F0.wireOp",EDGE,"E4.sketch_text.stroke-7"),sQuery(id+"F0.wireOp",EDGE,"E4.sketch_text.stroke-8"),sQuery(id+"F0.wireOp",EDGE,"E4.sketch_text.stroke-9"),sQuery(id+"F0.wireOp",EDGE,"E4.sketch_text.stroke-10"),sQuery(id+"F0.wireOp",EDGE,"E5.sketch_text.stroke-0"),sQuery(id+"F0.wireOp",EDGE,"E5.sketch_text.stroke-1"),sQuery(id+"F0.wireOp",EDGE,"E5.sketch_text.stroke-2"),sQuery(id+"F0.wireOp",EDGE,"E5.sketch_text.stroke-3"),sQuery(id+"F0.wireOp",EDGE,"E5.sketch_text.stroke-4"),sQuery(id+"F0.wireOp",EDGE,"E5.sketch_text.stroke-5"),sQuery(id+"F0.wireOp",EDGE,"E5.sketch_text.stroke-6"),sQuery(id+"F0.wireOp",EDGE,"E5.sketch_text.stroke-7"),sQuery(id+"F0.wireOp",EDGE,"E5.sketch_text.stroke-8"),sQuery(id+"F0.wireOp",EDGE,"E5.sketch_text.stroke-9"),sQuery(id+"F0.wireOp",EDGE,"E5.sketch_text.stroke-10"),sQuery(id+"F0.wireOp",EDGE,"E5.sketch_text.stroke-11"),sQuery(id+"F0.wireOp",EDGE,"E5.sketch_text.stroke-13"),sQuery(id+"F0.wireOp",EDGE,"E5.sketch_text.stroke-14"),sQuery(id+"F0.wireOp",EDGE,"E5.sketch_text.stroke-15"),sQuery(id+"F0.wireOp",EDGE,"E5.sketch_text.stroke-16"),sQuery(id+"F0.wireOp",EDGE,"E5.sketch_text.stroke-17"),sQuery(id+"F0.wireOp",EDGE,"E5.sketch_text.stroke-18"),sQuery(id+"F0.wireOp",EDGE,"E6.sketch_text.stroke-0"),sQuery(id+"F0.wireOp",EDGE,"E6.sketch_text.stroke-1"),sQuery(id+"F0.wireOp",EDGE,"E6.sketch_text.stroke-2"),sQuery(id+"F0.wireOp",EDGE,"E6.sketch_text.stroke-3"),sQuery(id+"F0.wireOp",EDGE,"E6.sketch_text.stroke-4"),sQuery(id+"F0.wireOp",EDGE,"E6.sketch_text.stroke-5"),sQuery(id+"F0.wireOp",EDGE,"E6.sketch_text.stroke-6"),sQuery(id+"F0.wireOp",EDGE,"E6.sketch_text.stroke-7"),sQuery(id+"F0.wireOp",EDGE,"E6.sketch_text.stroke-8")])]}),makeQuery(id+"F3.opExtrude","SWEPT_BODY",BODY,{"disambiguationData":[OSD([sQuery(id+"F2.wireOp",EDGE,"E7.sketch_text.stroke-0"),sQuery(id+"F2.wireOp",EDGE,"E7.sketch_text.stroke-1"),sQuery(id+"F2.wireOp",EDGE,"E7.sketch_text.stroke-2"),sQuery(id+"F2.wireOp",EDGE,"E7.sketch_text.stroke-3"),sQuery(id+"F2.wireOp",EDGE,"E7.sketch_text.stroke-5"),sQuery(id+"F2.wireOp",EDGE,"E7.sketch_text.stroke-6"),sQuery(id+"F2.wireOp",EDGE,"E7.sketch_text.stroke-7"),sQuery(id+"F2.wireOp",EDGE,"E7.sketch_text.stroke-8"),sQuery(id+"F2.wireOp",EDGE,"E7.sketch_text.stroke-9"),sQuery(id+"F2.wireOp",EDGE,"E7.sketch_text.stroke-10"),sQuery(id+"F2.wireOp",EDGE,"E7.sketch_text.stroke-11"),sQuery(id+"F2.wireOp",EDGE,"E7.sketch_text.stroke-13"),sQuery(id+"F2.wireOp",EDGE,"E7.sketch_text.stroke-14"),sQuery(id+"F2.wireOp",EDGE,"E8.sketch_text.stroke-0"),sQuery(id+"F2.wireOp",EDGE,"E8.sketch_text.stroke-1"),sQuery(id+"F2.wireOp",EDGE,"E8.sketch_text.stroke-2"),sQuery(id+"F2.wireOp",EDGE,"E8.sketch_text.stroke-3"),sQuery(id+"F2.wireOp",EDGE,"E8.sketch_text.stroke-4"),sQuery(id+"F2.wireOp",EDGE,"E8.sketch_text.stroke-5"),sQuery(id+"F2.wireOp",EDGE,"E8.sketch_text.stroke-6"),sQuery(id+"F2.wireOp",EDGE,"E8.sketch_text.stroke-7"),sQuery(id+"F2.wireOp",EDGE,"E8.sketch_text.stroke-8"),sQuery(id+"F2.wireOp",EDGE,"E8.sketch_text.stroke-9"),sQuery(id+"F2.wireOp",EDGE,"E8.sketch_text.stroke-10"),sQuery(id+"F2.wireOp",EDGE,"E8.sketch_text.stroke-11"),sQuery(id+"F2.wireOp",EDGE,"E8.sketch_text.stroke-12"),sQuery(id+"F2.wireOp",EDGE,"E8.sketch_text.stroke-13"),sQuery(id+"F2.wireOp",EDGE,"E8.sketch_text.stroke-14"),sQuery(id+"F2.wireOp",EDGE,"E8.sketch_text.stroke-15"),sQuery(id+"F2.wireOp",EDGE,"E8.sketch_text.stroke-16"),sQuery(id+"F2.wireOp",EDGE,"E8.sketch_text.stroke-17"),sQuery(id+"F2.wireOp",EDGE,"E8.sketch_text.stroke-18"),sQuery(id+"F2.wireOp",EDGE,"E9.sketch_text.stroke-0"),sQuery(id+"F2.wireOp",EDGE,"E9.sketch_text.stroke-1"),sQuery(id+"F2.wireOp",EDGE,"E9.sketch_text.stroke-2"),sQuery(id+"F2.wireOp",EDGE,"E9.sketch_text.stroke-3"),sQuery(id+"F2.wireOp",EDGE,"E9.sketch_text.stroke-4"),sQuery(id+"F2.wireOp",EDGE,"E9.sketch_text.stroke-5"),sQuery(id+"F2.wireOp",EDGE,"E9.sketch_text.stroke-6"),sQuery(id+"F2.wireOp",EDGE,"E9.sketch_text.stroke-7"),sQuery(id+"F2.wireOp",EDGE,"E9.sketch_text.stroke-8"),sQuery(id+"F2.wireOp",EDGE,"E9.sketch_text.stroke-9"),sQuery(id+"F2.wireOp",EDGE,"E9.sketch_text.stroke-10"),sQuery(id+"F2.wireOp",EDGE,"E10.sketch_text.stroke-0"),sQuery(id+"F2.wireOp",EDGE,"E10.sketch_text.stroke-1"),sQuery(id+"F2.wireOp",EDGE,"E10.sketch_text.stroke-2"),sQuery(id+"F2.wireOp",EDGE,"E10.sketch_text.stroke-3"),sQuery(id+"F2.wireOp",EDGE,"E10.sketch_text.stroke-4"),sQuery(id+"F2.wireOp",EDGE,"E10.sketch_text.stroke-5"),sQuery(id+"F2.wireOp",EDGE,"E10.sketch_text.stroke-6"),sQuery(id+"F2.wireOp",EDGE,"E10.sketch_text.stroke-7"),sQuery(id+"F2.wireOp",EDGE,"E10.sketch_text.stroke-8"),sQuery(id+"F2.wireOp",EDGE,"E10.sketch_text.stroke-9"),sQuery(id+"F2.wireOp",EDGE,"E10.sketch_text.stroke-10"),sQuery(id+"F2.wireOp",EDGE,"E10.sketch_text.stroke-11"),sQuery(id+"F2.wireOp",EDGE,"E11.sketch_text.stroke-0"),sQuery(id+"F2.wireOp",EDGE,"E11.sketch_text.stroke-1"),sQuery(id+"F2.wireOp",EDGE,"E11.sketch_text.stroke-2"),sQuery(id+"F2.wireOp",EDGE,"E11.sketch_text.stroke-3"),sQuery(id+"F2.wireOp",EDGE,"E11.sketch_text.stroke-4"),sQuery(id+"F2.wireOp",EDGE,"E11.sketch_text.stroke-6"),sQuery(id+"F2.wireOp",EDGE,"E11.sketch_text.stroke-7"),sQuery(id+"F2.wireOp",EDGE,"E12.sketch_text.stroke-0"),sQuery(id+"F2.wireOp",EDGE,"E12.sketch_text.stroke-1"),sQuery(id+"F2.wireOp",EDGE,"E12.sketch_text.stroke-2"),sQuery(id+"F2.wireOp",EDGE,"E12.sketch_text.stroke-3"),sQuery(id+"F2.wireOp",EDGE,"E13.sketch_text.stroke-0"),sQuery(id+"F2.wireOp",EDGE,"E13.sketch_text.stroke-1"),sQuery(id+"F2.wireOp",EDGE,"E13.sketch_text.stroke-2"),sQuery(id+"F2.wireOp",EDGE,"E13.sketch_text.stroke-3"),sQuery(id+"F2.wireOp",EDGE,"E13.sketch_text.stroke-4"),sQuery(id+"F2.wireOp",EDGE,"E13.sketch_text.stroke-5"),sQuery(id+"F2.wireOp",EDGE,"E13.sketch_text.stroke-6"),sQuery(id+"F2.wireOp",EDGE,"E13.sketch_text.stroke-7"),sQuery(id+"F2.wireOp",EDGE,"E13.sketch_text.stroke-8"),sQuery(id+"F2.wireOp",EDGE,"E13.sketch_text.stroke-9"),sQuery(id+"F2.wireOp",EDGE,"E14.sketch_text.stroke-0"),sQuery(id+"F2.wireOp",EDGE,"E14.sketch_text.stroke-1"),sQuery(id+"F2.wireOp",EDGE,"E14.sketch_text.stroke-2"),sQuery(id+"F2.wireOp",EDGE,"E14.sketch_text.stroke-3"),sQuery(id+"F2.wireOp",EDGE,"E14.sketch_text.stroke-4"),sQuery(id+"F2.wireOp",EDGE,"E14.sketch_text.stroke-5"),sQuery(id+"F2.wireOp",EDGE,"E14.sketch_text.stroke-6"),sQuery(id+"F2.wireOp",EDGE,"E14.sketch_text.stroke-7"),sQuery(id+"F2.wireOp",EDGE,"E14.sketch_text.stroke-8"),sQuery(id+"F2.wireOp",EDGE,"E14.sketch_text.stroke-9"),sQuery(id+"F2.wireOp",EDGE,"E14.sketch_text.stroke-10"),sQuery(id+"F2.wireOp",EDGE,"E14.sketch_text.stroke-11")])]})]});
            booleanBodies(context, id + "F7", {"operationType" : BooleanOperationType.SUBTRACTION, "tools" : qUnion([Q0, Q1]), "targets" : qUnion([Q2])});
        }
    });
